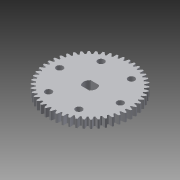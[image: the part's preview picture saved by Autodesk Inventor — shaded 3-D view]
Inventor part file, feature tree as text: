
AUTODESK INVENTOR PART (.ipt)
format: ipt  version: 2013 (Build 170138000, 138)  size: 433,152 bytes
history: native  units: in
note: dims shown in document units (in); Inventor stores cm internally (conversion verified against a paired STEP export)
features: extrude x1, sketch x1
ambient origin geometry x8: Origin, YZ Plane, XZ Plane, XY Plane, X Axis, Y Axis, Z Axis, Center Point
bodies: Solid1 (feature_tree)
feature tree (2):
  extrude  "Extrusion1"  Depth=0.1968in
  sketch  "Sketch1"  dims[d0=0.2955in d2=0.1968in d3=0.1968in d4=0.2598in d5=1.175in d6=0.5996in d7=0.1894in d8=0.25in d9=0.0in]
